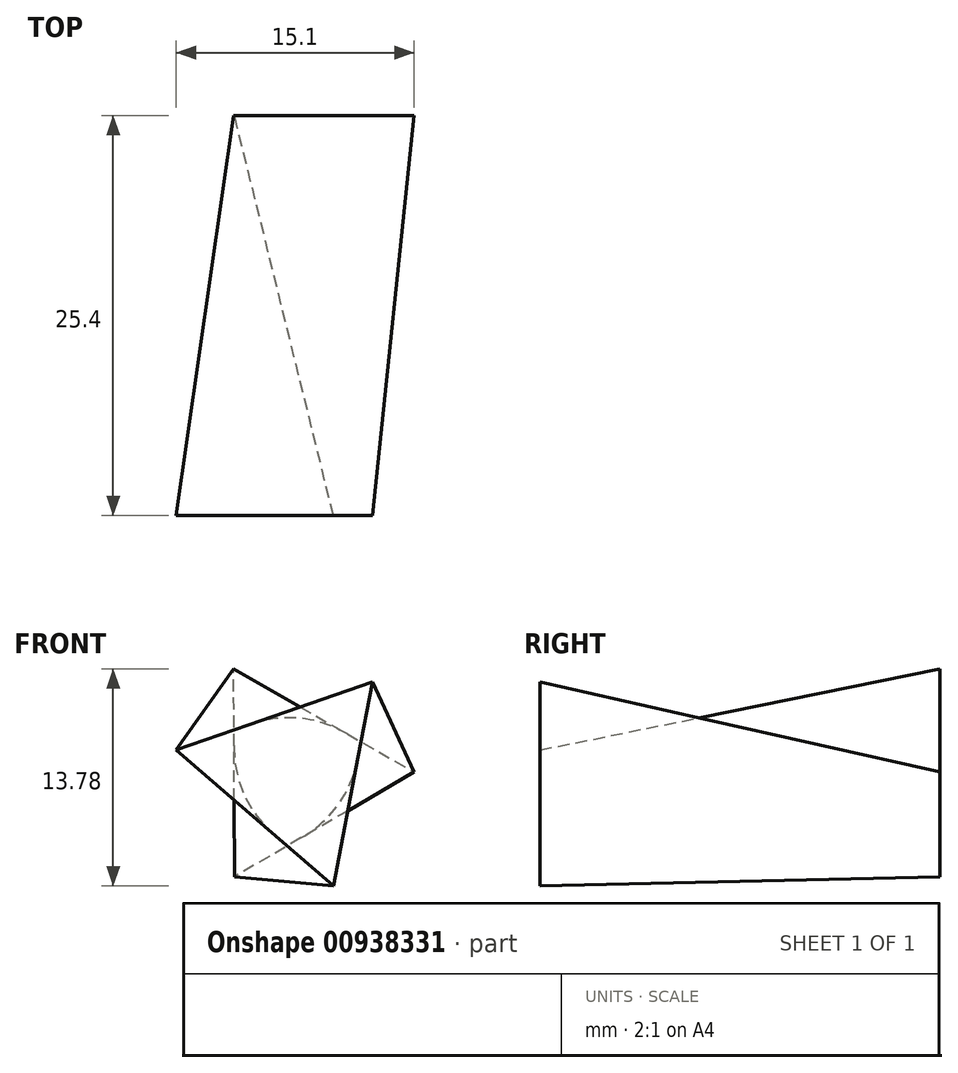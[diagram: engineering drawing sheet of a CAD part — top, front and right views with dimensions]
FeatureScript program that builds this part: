
annotation { "Feature Type Name" : "Feature", "Feature Type Description" : "" }
export const myFeature = defineFeature(function(context is Context, id is Id, definition is map)
    precondition{}
    {
        {
            var Q0;
            Q0=qCreatedBy(makeId("Front.planeOp"),FACE);
            var sketch = newSketch(context, id + "F0", { "sketchPlane" : qUnion([Q0])});
            skCircle(sketch, "E0.cCircle", {"center": v(0, 0) * mm, "radius": 3.8 * mm, "construction": true});
            skLineSegment(sketch, "E0.0", {"start": v(-3.84, 6.58) * mm, "end": v(7.62, 0.03) * mm});
            skLineSegment(sketch, "E0.1", {"start": v(7.62, 0.03) * mm, "end": v(-3.78, -6.61) * mm});
            skLineSegment(sketch, "E0.2", {"start": v(-3.78, -6.61) * mm, "end": v(-3.84, 6.58) * mm});
            skPoint(sketch, "E0.0.midPoint", {"position": v(1.9, 3.3) * mm});
            skSolve(sketch);
        }
        {
            var Q0;
            Q0=qCreatedBy(makeId("Front.planeOp"),FACE);
            cPlane(context, id + "F1", {"entities" : qUnion([Q0]), "cplaneType" : CPlaneType.OFFSET, "offset" : 25.4 * mm, "width" : 152.4 * mm, "height" : 152.4 * mm});
        }
        {
            var Q0;
            Q0=qCreatedBy(id+"F1.planeOp",FACE);
            var sketch = newSketch(context, id + "F2", { "sketchPlane" : qUnion([Q0])});
            skCircle(sketch, "E1.cCircle", {"center": v(0, 0) * mm, "radius": 3.81 * mm, "construction": true});
            skLineSegment(sketch, "E1.0", {"start": v(4.98, 5.76) * mm, "end": v(2.5, -7.2) * mm});
            skLineSegment(sketch, "E1.1", {"start": v(2.5, -7.2) * mm, "end": v(-7.48, 1.43) * mm});
            skLineSegment(sketch, "E1.2", {"start": v(-7.48, 1.43) * mm, "end": v(4.98, 5.76) * mm});
            skPoint(sketch, "E1.0.midPoint", {"position": v(3.74, -0.72) * mm});
            skSolve(sketch);
        }
        {
            var Q0;
            Q0=makeQuery(id+"F2.imprint","IMPRINT",FACE,{"disambiguationData":[TD([[makeQuery(id+"F2.imprint","IMPRINT",EDGE,{"derivedFrom":sQuery(id+"F2.wireOp",EDGE,"E1.0")}),-1.0]])]});
            var Q1;
            Q1=makeQuery(id+"F0.imprint","IMPRINT",FACE,{"disambiguationData":[TD([[makeQuery(id+"F0.imprint","IMPRINT",EDGE,{"derivedFrom":sQuery(id+"F0.wireOp",EDGE,"E0.0")}),-1.0]])]});
            loft(context, id + "F3", {"sheetProfilesArray" : [{ "sheetProfileEntities" : qUnion([Q0]) }, { "sheetProfileEntities" : qUnion([Q1]) }]});
        }
    });
